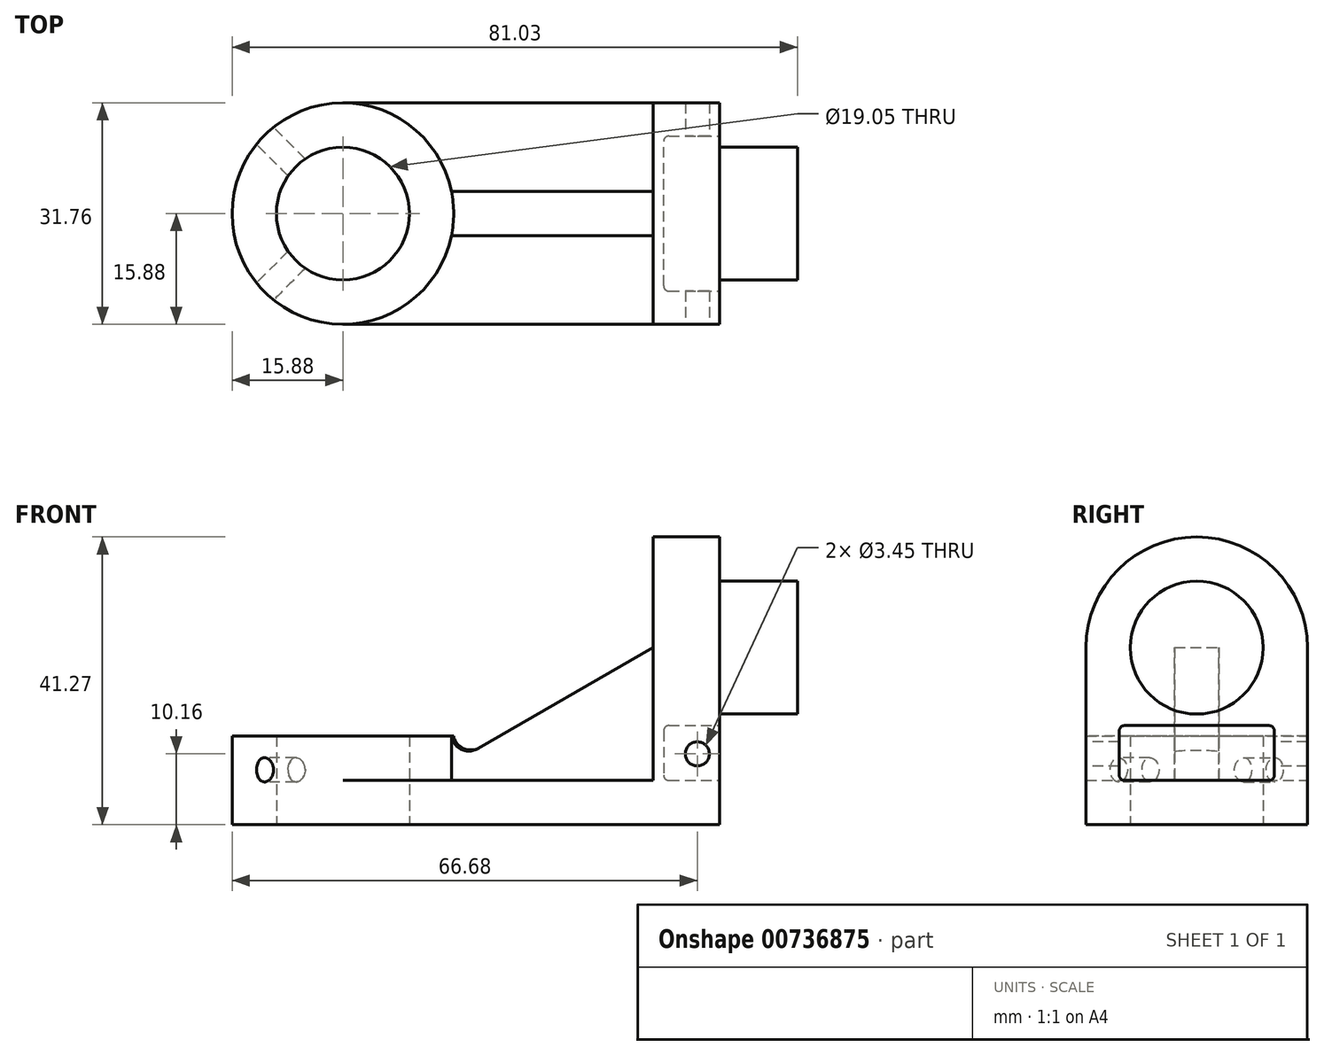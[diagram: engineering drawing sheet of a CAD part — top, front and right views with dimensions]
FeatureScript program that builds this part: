
annotation { "Feature Type Name" : "Feature", "Feature Type Description" : "" }
export const myFeature = defineFeature(function(context is Context, id is Id, definition is map)
    precondition{}
    {
        {
            var Q0;
            Q0=qCreatedBy(makeId("Top.planeOp"),FACE);
            var sketch = newSketch(context, id + "F0", { "sketchPlane" : qUnion([Q0])});
            skCircle(sketch, "E0", {"center": v(0, 0) * mm, "radius": 15.88 * mm});
            skCircle(sketch, "E1", {"center": v(0, 0) * mm, "radius": 9.53 * mm});
            skSolve(sketch);
        }
        {
            var Q0;
            Q0 = qSketchRegion(id + "F0", true);
            extrude(context, id + "F1", {"entities" : qUnion([Q0]), "depth" : 12.7 * mm, "offsetDistance" : 25.4 * mm});
        }
        {
            var Q0;
            Q0=qCreatedBy(makeId("Top.planeOp"),FACE);
            var sketch = newSketch(context, id + "F2", { "sketchPlane" : qUnion([Q0])});
            skArc(sketch, "E2.0", {"start": v(0, -15.88) * mm, "mid": v(15.88, 0) * mm, "end": v(0, 15.88) * mm});
            skLineSegment(sketch, "E3", {"start": v(0, 15.88) * mm, "end": v(53.98, 15.88) * mm});
            skLineSegment(sketch, "E4", {"start": v(53.98, 15.88) * mm, "end": v(53.98, -15.87) * mm});
            skLineSegment(sketch, "E5", {"start": v(53.98, -15.87) * mm, "end": v(0, -15.88) * mm});
            skSolve(sketch);
        }
        {
            var Q0;
            Q0 = qSketchRegion(id + "F2", true);
            extrude(context, id + "F3", {"entities" : qUnion([Q0]), "operationType" : NewBodyOperationType.ADD, "depth" : 6.35 * mm, "offsetDistance" : 25.4 * mm});
        }
        {
            var Q0;
            Q0=makeQuery(id+"F3.opExtrude","SWEPT_FACE",FACE,{"disambiguationData":[OSD([sQuery(id+"F2.wireOp",EDGE,"E4")])]});
            var sketch = newSketch(context, id + "F4", { "sketchPlane" : qUnion([Q0])});
            skLineSegment(sketch, "E6", {"start": v(0, 6.35) * mm, "end": v(0, 25.4) * mm, "construction": true});
            skArc(sketch, "E7", {"start": v(15.87, 25.4) * mm, "mid": v(0, 41.27) * mm, "end": v(-15.88, 25.4) * mm});
            skLineSegment(sketch, "E8", {"start": v(-15.88, 6.35) * mm, "end": v(-15.88, 25.4) * mm});
            skLineSegment(sketch, "E9", {"start": v(15.87, 6.35) * mm, "end": v(15.87, 25.4) * mm});
            skLineSegment(sketch, "E10", {"start": v(-15.88, 6.35) * mm, "end": v(15.87, 6.35) * mm});
            skSolve(sketch);
        }
        {
            var Q0;
            Q0 = qSketchRegion(id + "F4", true);
            extrude(context, id + "F5", {"entities" : qUnion([Q0]), "operationType" : NewBodyOperationType.ADD, "oppositeDirection" : true, "depth" : 9.52 * mm, "offsetDistance" : 25.4 * mm});
        }
        {
            var Q0;
            Q0=makeQuery(id+"F5.boolean.opBoolean","MERGE",FACE,{"derivedFrom":[makeQuery(id+"F3.opExtrude","SWEPT_FACE",FACE,{"disambiguationData":[OSD([sQuery(id+"F2.wireOp",EDGE,"E4")])]}),makeQuery(id+"F5.opExtrude","CAP_FACE",FACE,{"disambiguationData":[OSD([sQuery(id+"F4.wireOp",EDGE,"E7"),sQuery(id+"F4.wireOp",EDGE,"E8"),sQuery(id+"F4.wireOp",EDGE,"E9"),sQuery(id+"F4.wireOp",EDGE,"E10")])],"isStart":true})]});
            var sketch = newSketch(context, id + "F6", { "sketchPlane" : qUnion([Q0])});
            skCircle(sketch, "E11", {"center": v(0, 25.4) * mm, "radius": 9.53 * mm});
            skSolve(sketch);
        }
        {
            var Q0;
            Q0 = qSketchRegion(id + "F6", true);
            extrude(context, id + "F7", {"entities" : qUnion([Q0]), "operationType" : NewBodyOperationType.ADD, "depth" : 11.18 * mm, "offsetDistance" : 25.4 * mm});
        }
        {
            var Q0;
            Q0=makeQuery(id+"F5.boolean.opBoolean","MERGE",FACE,{"derivedFrom":[makeQuery(id+"F3.opExtrude","SWEPT_FACE",FACE,{"disambiguationData":[OSD([sQuery(id+"F2.wireOp",EDGE,"E4")])]}),makeQuery(id+"F5.opExtrude","CAP_FACE",FACE,{"disambiguationData":[OSD([sQuery(id+"F4.wireOp",EDGE,"E7"),sQuery(id+"F4.wireOp",EDGE,"E8"),sQuery(id+"F4.wireOp",EDGE,"E9"),sQuery(id+"F4.wireOp",EDGE,"E10")])],"isStart":true})]});
            var sketch = newSketch(context, id + "F8", { "sketchPlane" : qUnion([Q0])});
            skLineSegment(sketch, "E12.bottom", {"start": v(-11.11, 14.22) * mm, "end": v(11.11, 14.22) * mm});
            skLineSegment(sketch, "E12.top", {"start": v(-11.11, 6.35) * mm, "end": v(11.11, 6.35) * mm});
            skLineSegment(sketch, "E12.left", {"start": v(-11.11, 14.22) * mm, "end": v(-11.11, 6.35) * mm});
            skLineSegment(sketch, "E12.right", {"start": v(11.11, 14.22) * mm, "end": v(11.11, 6.35) * mm});
            skSolve(sketch);
        }
        {
            var Q0;
            Q0 = qSketchRegion(id + "F8", true);
            extrude(context, id + "F9", {"entities" : qUnion([Q0]), "operationType" : NewBodyOperationType.REMOVE, "oppositeDirection" : true, "depth" : 8 * mm, "offsetDistance" : 25.4 * mm});
        }
        {
            var Q0;
            Q0=makeQuery(id+"F5.boolean.opBoolean","MERGE",FACE,{"derivedFrom":[makeQuery(id+"F3.opExtrude","SWEPT_FACE",FACE,{"disambiguationData":[OSD([sQuery(id+"F2.wireOp",EDGE,"E5")])]}),makeQuery(id+"F5.opExtrude","SWEPT_FACE",FACE,{"disambiguationData":[OSD([sQuery(id+"F4.wireOp",EDGE,"E8")])]})]});
            var sketch = newSketch(context, id + "F10", { "sketchPlane" : qUnion([Q0])});
            skCircle(sketch, "E13", {"center": v(50.8, 10.16) * mm, "radius": 1.73 * mm});
            skSolve(sketch);
        }
        {
            var Q0;
            Q0 = qSketchRegion(id + "F10", true);
            extrude(context, id + "F11", {"entities" : qUnion([Q0]), "operationType" : NewBodyOperationType.REMOVE, "endBound" : BoundingType.THROUGH_ALL, "oppositeDirection" : true, "depth" : 25.4 * mm, "offsetDistance" : 25.4 * mm});
        }
        {
            var Q0;
            Q0=qCreatedBy(makeId("Front.planeOp"),FACE);
            var sketch = newSketch(context, id + "F12", { "sketchPlane" : qUnion([Q0])});
            skLineSegment(sketch, "E14", {"start": v(44.45, 25.4) * mm, "end": v(11.45, 6.35) * mm});
            skLineSegment(sketch, "E15.0", {"start": v(44.45, 6.35) * mm, "end": v(44.45, 25.4) * mm});
            skLineSegment(sketch, "E15.1", {"start": v(44.45, 6.35) * mm, "end": v(11.45, 6.35) * mm});
            skPoint(sketch, "E16.orphan", {"position": v(0, 6.35) * mm});
            skSolve(sketch);
        }
        {
            var Q0;
            Q0 = qSketchRegion(id + "F12", true);
            extrude(context, id + "F13", {"entities" : qUnion([Q0]), "operationType" : NewBodyOperationType.ADD, "endBound" : BoundingType.SYMMETRIC, "depth" : 6.35 * mm, "offsetDistance" : 25.4 * mm});
        }
        {
            var Q0;
            Q0=makeQuery(id+"F13.boolean.opBoolean","INTERSECT",EDGE,{"derivedFrom":[makeQuery(id+"F1.opExtrude","SWEPT_FACE",FACE,{"disambiguationData":[OSD([sQuery(id+"F0.wireOp",EDGE,"E0")])]}),makeQuery(id+"F13.opExtrude","SWEPT_FACE",FACE,{"disambiguationData":[OSD([sQuery(id+"F12.wireOp",EDGE,"E14")])]})]});
            fillet(context, id + "F14", {"entities" : qUnion([Q0]), "radius" : 2.54 * mm, "tangentPropagation" : true, "allowEdgeOverflow" : false});
        }
        {
            var Q0;
            Q0=makeQuery(id+"F13.opExtrude","CAP_EDGE",EDGE,{"disambiguationData":[OSD([sQuery(id+"F12.wireOp",EDGE,"E15.0")])],"isStart":false});
            var Q1;
            Q1=makeQuery(id+"F13.opExtrude","CAP_EDGE",EDGE,{"disambiguationData":[OSD([sQuery(id+"F12.wireOp",EDGE,"E15.0")])],"isStart":true});
            var Q2;
            Q2=makeQuery(id+"F9.boolean.opBoolean","COPY",EDGE,{"derivedFrom":makeQuery(id+"F9.opExtrude","CAP_EDGE",EDGE,{"disambiguationData":[OSD([sQuery(id+"F8.wireOp",EDGE,"E12.top")])],"isStart":false})});
            var Q3;
            Q3=makeQuery(id+"F9.boolean.opBoolean","COPY",EDGE,{"derivedFrom":makeQuery(id+"F9.opExtrude","CAP_EDGE",EDGE,{"disambiguationData":[OSD([sQuery(id+"F8.wireOp",EDGE,"E12.right")])],"isStart":false})});
            var Q4;
            Q4=makeQuery(id+"F9.boolean.opBoolean","COPY",EDGE,{"derivedFrom":makeQuery(id+"F9.opExtrude","SWEPT_EDGE",EDGE,{"disambiguationData":[OSD([sQuery(id+"F8.wireOp",EDGE,"E12.top"),sQuery(id+"F8.wireOp",EDGE,"E12.right")])]})});
            var Q5;
            Q5=makeQuery(id+"F9.boolean.opBoolean","COPY",EDGE,{"derivedFrom":makeQuery(id+"F9.opExtrude","SWEPT_EDGE",EDGE,{"disambiguationData":[OSD([sQuery(id+"F8.wireOp",EDGE,"E12.bottom"),sQuery(id+"F8.wireOp",EDGE,"E12.right")])]})});
            var Q6;
            Q6=makeQuery(id+"F9.boolean.opBoolean","COPY",EDGE,{"derivedFrom":makeQuery(id+"F9.opExtrude","CAP_EDGE",EDGE,{"disambiguationData":[OSD([sQuery(id+"F8.wireOp",EDGE,"E12.bottom")])],"isStart":false})});
            var Q7;
            Q7=makeQuery(id+"F9.boolean.opBoolean","COPY",EDGE,{"derivedFrom":makeQuery(id+"F9.opExtrude","SWEPT_EDGE",EDGE,{"disambiguationData":[OSD([sQuery(id+"F8.wireOp",EDGE,"E12.bottom"),sQuery(id+"F8.wireOp",EDGE,"E12.left")])]})});
            var Q8;
            Q8=makeQuery(id+"F9.boolean.opBoolean","COPY",EDGE,{"derivedFrom":makeQuery(id+"F9.opExtrude","SWEPT_EDGE",EDGE,{"disambiguationData":[OSD([sQuery(id+"F8.wireOp",EDGE,"E12.top"),sQuery(id+"F8.wireOp",EDGE,"E12.left")])]})});
            var Q9;
            Q9=makeQuery(id+"F9.boolean.opBoolean","COPY",EDGE,{"derivedFrom":makeQuery(id+"F9.opExtrude","CAP_EDGE",EDGE,{"disambiguationData":[OSD([sQuery(id+"F8.wireOp",EDGE,"E12.left")])],"isStart":false})});
            fillet(context, id + "F15", {"entities" : qUnion([Q0, Q1, Q2, Q3, Q4, Q5, Q6, Q7, Q8, Q9]), "radius" : 0.76 * mm, "tangentPropagation" : true, "allowEdgeOverflow" : false});
        }
        {
            var Q0;
            Q0=makeQuery(id+"F3.boolean.opBoolean","MERGE",FACE,{"derivedFrom":[makeQuery(id+"F1.opExtrude","CAP_FACE",FACE,{"disambiguationData":[OSD([sQuery(id+"F0.wireOp",EDGE,"E0"),sQuery(id+"F0.wireOp",EDGE,"E1")])],"isStart":true}),makeQuery(id+"F3.opExtrude","CAP_FACE",FACE,{"disambiguationData":[OSD([sQuery(id+"F2.wireOp",EDGE,"E2.0"),sQuery(id+"F2.wireOp",EDGE,"E3"),sQuery(id+"F2.wireOp",EDGE,"E4"),sQuery(id+"F2.wireOp",EDGE,"E5")])],"isStart":true})]});
            var sketch = newSketch(context, id + "F16", { "sketchPlane" : qUnion([Q0])});
            skLineSegment(sketch, "E17", {"start": v(0, 0) * mm, "end": v(-23.44, 0) * mm});
            skPoint(sketch, "E17.endSnap0", {"position": v(-15.88, 0) * mm});
            skLineSegment(sketch, "E18", {"start": v(-23.44, 0) * mm, "end": v(0, -23.44) * mm});
            skLineSegment(sketch, "E19", {"start": v(-23.44, 0) * mm, "end": v(0, 23.44) * mm});
            skSolve(sketch);
        }
        {
            var Q0;
            Q0=sQuery(id+"F16.wireOp",EDGE,"E19");
            cPlane(context, id + "F17", {"entities" : qUnion([Q0]), "cplaneType" : CPlaneType.LINE_ANGLE, "offset" : 25.4 * mm, "angle" : 90 * degree, "width" : 152.4 * mm, "height" : 152.4 * mm});
        }
        {
            var Q0;
            Q0=qCreatedBy(id+"F17.planeOp",FACE);
            var sketch = newSketch(context, id + "F18", { "sketchPlane" : qUnion([Q0])});
            skCircle(sketch, "E20", {"center": v(0, 7.87) * mm, "radius": 1.73 * mm});
            skSolve(sketch);
        }
        {
            var Q0;
            Q0 = qSketchRegion(id + "F18", true);
            extrude(context, id + "F19", {"entities" : qUnion([Q0]), "operationType" : NewBodyOperationType.REMOVE, "depth" : 8.9 * mm, "offsetDistance" : 25.4 * mm});
        }
        {
            var Q0;
            Q0=sQuery(id+"F16.wireOp",EDGE,"E18");
            cPlane(context, id + "F20", {"entities" : qUnion([Q0]), "cplaneType" : CPlaneType.LINE_ANGLE, "offset" : 25.4 * mm, "angle" : 90 * degree, "width" : 152.4 * mm, "height" : 152.4 * mm});
        }
        {
            var Q0;
            Q0=qCreatedBy(id+"F20.planeOp",FACE);
            var sketch = newSketch(context, id + "F21", { "sketchPlane" : qUnion([Q0])});
            skCircle(sketch, "E21", {"center": v(0, 7.87) * mm, "radius": 1.73 * mm});
            skSolve(sketch);
        }
        {
            var Q0;
            Q0 = qSketchRegion(id + "F21", true);
            extrude(context, id + "F22", {"entities" : qUnion([Q0]), "operationType" : NewBodyOperationType.REMOVE, "depth" : 11.33 * mm, "offsetDistance" : 25.4 * mm});
        }
    });
